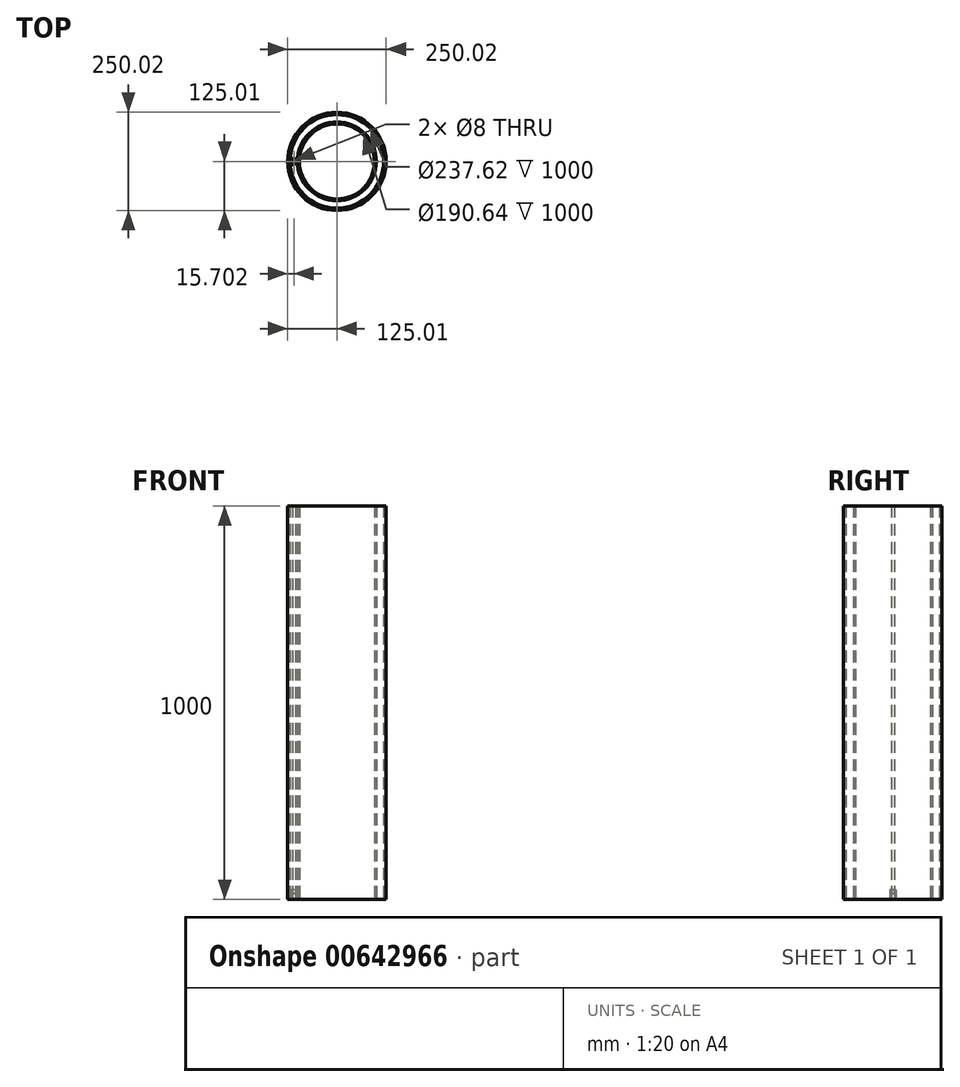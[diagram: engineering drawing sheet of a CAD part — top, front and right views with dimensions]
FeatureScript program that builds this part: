
annotation { "Feature Type Name" : "Feature", "Feature Type Description" : "" }
export const myFeature = defineFeature(function(context is Context, id is Id, definition is map)
    precondition{}
    {
        {
            var Q0;
            Q0=qCreatedBy(makeId("Top.planeOp"),FACE);
            var sketch = newSketch(context, id + "F0", { "sketchPlane" : qUnion([Q0])});
            skCircle(sketch, "E0", {"center": v(0, 0) * mm, "radius": 125 * mm});
            skCircle(sketch, "E1", {"center": v(0, 0) * mm, "radius": 100.22 * mm});
            skCircle(sketch, "E2.0", {"center": v(0, 0) * mm, "radius": 118.8 * mm});
            skCircle(sketch, "E3.0", {"center": v(0, 0) * mm, "radius": 95.32 * mm});
            skCircle(sketch, "E4", {"center": v(-109.3, 0) * mm, "radius": 4 * mm});
            skCircle(sketch, "E5", {"center": v(-109.3, 0) * mm, "radius": 7.5 * mm});
            skLineSegment(sketch, "E6", {"start": v(-109.3, 7.5) * mm, "end": v(-118.57, 7.5) * mm});
            skLineSegment(sketch, "E7", {"start": v(-109.3, -7.5) * mm, "end": v(-118.57, -7.5) * mm});
            skSolve(sketch);
        }
        {
            var Q0;
            Q0=makeQuery(id+"F0.imprint","IMPRINT",FACE,{"disambiguationData":[TD([[makeQuery(id+"F0.imprint","IMPRINT",EDGE,{"derivedFrom":sQuery(id+"F0.wireOp",EDGE,"E1")}),1.0]])]});
            extrude(context, id + "F1", {"entities" : qUnion([Q0]), "depth" : 1000 * mm, "offsetDistance" : 25 * mm});
        }
        {
            var Q0;
            Q0=makeQuery(id+"F0.imprint","IMPRINT",FACE,{"disambiguationData":[TD([[makeQuery(id+"F0.imprint","IMPRINT",EDGE,{"derivedFrom":sQuery(id+"F0.wireOp",EDGE,"E4")}),1.0]])]});
            extrude(context, id + "F2", {"entities" : qUnion([Q0]), "depth" : 1000 * mm, "offsetDistance" : 25 * mm});
        }
        {
            var Q0;
            Q0=makeQuery(id+"F0.imprint","IMPRINT",FACE,{"disambiguationData":[TD([[makeQuery(id+"F0.imprint","IMPRINT",EDGE,{"derivedFrom":sQuery(id+"F0.wireOp",EDGE,"E4")}),-1.0]])]});
            var Q1;
            Q1=sQuery(id+"F0.wireOp",EDGE,"E4");
            var Q2;
            Q2=sQuery(id+"F0.wireOp",EDGE,"E5");
            extrude(context, id + "F3", {"entities" : qUnion([Q0]), "surfaceEntities" : qUnion([Q1, Q2]), "depth" : 24 * mm, "offsetDistance" : 25 * mm});
        }
        {
            var Q0;
            Q0=makeQuery(id+"F0.imprint","IMPRINT",FACE,{"disambiguationData":[TD([[makeQuery(id+"F0.imprint","IMPRINT",EDGE,{"derivedFrom":sQuery(id+"F0.wireOp",EDGE,"E0")}),1.0]])]});
            extrude(context, id + "F4", {"entities" : qUnion([Q0]), "depth" : 1000 * mm, "offsetDistance" : 25 * mm});
        }
        {
            var Q0;
            {var subQ0=sQuery(id+"F0.wireOp",EDGE,"E6");Q0=makeQuery(id+"F0.imprint","IMPRINT",FACE,{"disambiguationData":[TD([[makeQuery(id+"F0.imprint","IMPRINT",EDGE,{"derivedFrom":subQ0}),1.0]])]});}
            var Q1;
            Q1=makeQuery(id+"F0.imprint","IMPRINT",FACE,{"disambiguationData":[TD([[makeQuery(id+"F0.imprint","IMPRINT",EDGE,{"derivedFrom":sQuery(id+"F0.wireOp",EDGE,"E4")}),-1.0]])]});
            extrude(context, id + "F5", {"entities" : qUnion([Q0, Q1]), "depth" : 15 * mm, "offsetDistance" : 25 * mm});
        }
    });
